# Revit family: Диван-качели садовые «Лиана» Арт 16021
name_source: partatom
category: Антураж
revit_build: Autodesk Revit 2018 (Build: 20180423_1000(x64)
units: mm (PartAtom-declared; Revit-internal decimal feet)

## family parameters
Всегда вертикально = Да
Источник визуального образа = Геометрия семейства
На основе рабочей плоскости = Нет
Общий = Нет
При загрузке вырезать с полостями = Нет
Точка расчета площади = Нет

## types (2) — shared parameters
URL = https://hobbyka.ru
Артикул товара = Арт. 16021
Высота = 1895 мм
Группа модели = Садовая и дачная мебель
Длина = 1800 мм
Изготовитель = ООО «Хоббика»
Изображение типоразмера = Диван-качели садовые «Лиана» Арт 16021.jpg
Материал изделия = Дерево
Текстиль = <По категории>
Цвет отделки = Дерево
Ширина = 633 мм

## per-type parameters (varying)
| type | Без матраса и подушек | С матрасом и подушками |
| Диван-качели садовые «Лиана». Версия с матрасом и подушками | Нет | Да |
| Диван-качели садовые «Лиана». Версия без матраса и подушек | Да | Нет |

note: column(s) folded — value = type name in every type: Описание
